FCSTD DOCUMENT  (FreeCAD 0.16R6706 (Git))
Label: Taster_3fach_Unterbau
License: All rights reserved
LicenseURL: http://en.wikipedia.org/wiki/All_rights_reserved
objects: Sketcher::SketchObject×1
note: 1 computed .brp shape members not serialized (recipe doc carries the construction recipe); baked Part::Feature solids carry a one-line shape summary decoded from their .brp

FEATURE [Sketcher::SketchObject] Sketch
  sketch-geometry (51):
    g0: LineSegment StartX=6.07199 StartY=33.4504 StartZ=0 EndX=20.072 EndY=33.4504 EndZ=0
    g1: LineSegment StartX=20.072 StartY=33.4504 StartZ=0 EndX=20.072 EndY=58.5504 EndZ=0
    g2: LineSegment StartX=20.072 StartY=58.5504 StartZ=0 EndX=24.072 EndY=58.5504 EndZ=0
    g3: LineSegment StartX=24.072 StartY=58.5504 StartZ=0 EndX=24.072 EndY=33.4504 EndZ=0
    g4: LineSegment StartX=24.072 StartY=33.4504 StartZ=0 EndX=38.072 EndY=33.4504 EndZ=0
    g5: LineSegment StartX=38.072 StartY=33.4504 StartZ=0 EndX=38.072 EndY=58.5504 EndZ=0
    g6: LineSegment StartX=38.072 StartY=58.5504 StartZ=0 EndX=42.072 EndY=58.5504 EndZ=0
    g7: LineSegment StartX=42.072 StartY=58.5504 StartZ=0 EndX=42.072 EndY=33.4504 EndZ=0
    g8: LineSegment StartX=42.072 StartY=33.4504 StartZ=0 EndX=56.072 EndY=33.4504 EndZ=0
    g9: LineSegment StartX=6.07199 StartY=27.4504 StartZ=0 EndX=20.072 EndY=27.4504 EndZ=0
    g10: LineSegment StartX=20.072 StartY=27.4504 StartZ=0 EndX=20.072 EndY=2.35037 EndZ=0
    g11: LineSegment StartX=20.072 StartY=2.35037 StartZ=0 EndX=24.072 EndY=2.35037 EndZ=0
    g12: LineSegment StartX=24.072 StartY=2.35037 StartZ=0 EndX=24.072 EndY=27.4504 EndZ=0
    g13: LineSegment StartX=24.072 StartY=27.4504 StartZ=0 EndX=38.072 EndY=27.4504 EndZ=0
    g14: LineSegment StartX=38.072 StartY=27.4504 StartZ=0 EndX=38.072 EndY=2.35037 EndZ=0
    g15: LineSegment StartX=38.072 StartY=2.35037 StartZ=0 EndX=42.072 EndY=2.35037 EndZ=0
    g16: LineSegment StartX=42.072 StartY=2.35037 StartZ=0 EndX=42.072 EndY=27.4504 EndZ=0
    g17: LineSegment StartX=42.072 StartY=27.4504 StartZ=0 EndX=56.072 EndY=27.4504 EndZ=0
    g18: LineSegment [constr] StartX=20.072 StartY=33.4504 StartZ=0 EndX=20.072 EndY=27.4504 EndZ=0
    g19: LineSegment StartX=56.072 StartY=33.4504 StartZ=0 EndX=56.072 EndY=45.4504 EndZ=0
    g20: LineSegment StartX=56.072 StartY=27.4504 StartZ=0 EndX=56.072 EndY=15.4504 EndZ=0
    g21: LineSegment StartX=6.07199 StartY=33.4504 StartZ=0 EndX=6.07199 EndY=45.4504 EndZ=0
    g22: LineSegment StartX=6.07199 StartY=27.4504 StartZ=0 EndX=6.07199 EndY=15.4504 EndZ=0
    g23: LineSegment StartX=59.272 StartY=45.4504 StartZ=0 EndX=59.272 EndY=15.4504 EndZ=0
    g24: LineSegment StartX=2.87199 StartY=45.4504 StartZ=0 EndX=2.87199 EndY=15.4504 EndZ=0
    g25: LineSegment [constr] StartX=56.072 StartY=45.4504 StartZ=0 EndX=59.272 EndY=45.4504 EndZ=0
    g26: LineSegment StartX=56.072 StartY=45.4504 StartZ=0 EndX=56.372 EndY=58.5504 EndZ=0
    g27: LineSegment StartX=59.272 StartY=45.4504 StartZ=0 EndX=59.872 EndY=56.9724 EndZ=0
    g28: LineSegment StartX=56.372 StartY=58.5504 StartZ=0 EndX=58.374 EndY=58.5504 EndZ=0
    g29: ArcOfCircle CenterX=58.374 CenterY=57.0504 CenterZ=0 NormalX=0 NormalY=0 NormalZ=1 Radius=1.5 StartAngle=6.23116 EndAngle=7.85398
    g30: LineSegment [constr] StartX=42.072 StartY=58.5504 StartZ=0 EndX=56.372 EndY=58.5504 EndZ=0
    g31: LineSegment StartX=56.072 StartY=15.4504 StartZ=0 EndX=56.372 EndY=2.35037 EndZ=0
    g32: LineSegment StartX=59.272 StartY=15.4504 StartZ=0 EndX=59.872 EndY=3.92838 EndZ=0
    g33: LineSegment StartX=56.372 StartY=2.35037 StartZ=0 EndX=58.374 EndY=2.35037 EndZ=0
    g34: ArcOfCircle CenterX=58.374 CenterY=3.85037 CenterZ=0 NormalX=0 NormalY=0 NormalZ=1 Radius=1.5 StartAngle=4.71239 EndAngle=6.33521
    g35: LineSegment [constr] StartX=42.072 StartY=2.35037 StartZ=0 EndX=56.372 EndY=2.35037 EndZ=0
    g36: LineSegment [constr] StartX=20.072 StartY=2.35037 StartZ=0 EndX=5.77199 EndY=2.35037 EndZ=0
    g37: LineSegment StartX=6.07199 StartY=15.4504 StartZ=0 EndX=5.77199 EndY=2.35037 EndZ=0
    g38: LineSegment StartX=2.87199 StartY=15.4504 StartZ=0 EndX=2.27199 EndY=3.92838 EndZ=0
    g39: LineSegment StartX=6.07199 StartY=45.4504 StartZ=0 EndX=5.77199 EndY=58.5504 EndZ=0
    g40: LineSegment StartX=2.87199 StartY=45.4504 StartZ=0 EndX=2.27199 EndY=56.9724 EndZ=0
    g41: LineSegment StartX=5.77199 StartY=58.5504 StartZ=0 EndX=3.76996 EndY=58.5504 EndZ=0
    g42: LineSegment StartX=5.77199 StartY=2.35037 StartZ=0 EndX=3.76996 EndY=2.35037 EndZ=0
    g43: LineSegment [constr] StartX=20.072 StartY=58.5504 StartZ=0 EndX=5.77199 EndY=58.5504 EndZ=0
    g44: ArcOfCircle CenterX=3.76996 CenterY=3.85037 CenterZ=0 NormalX=0 NormalY=0 NormalZ=1 Radius=1.5 StartAngle=3.08957 EndAngle=4.71239
    g45: ArcOfCircle CenterX=3.76996 CenterY=57.0504 CenterZ=0 NormalX=0 NormalY=0 NormalZ=1 Radius=1.5 StartAngle=1.5708 EndAngle=3.19362
    g46: LineSegment [constr] StartX=2.27199 StartY=56.9724 StartZ=0 EndX=5.80812 EndY=56.9724 EndZ=0
    g47: LineSegment [constr] StartX=59.872 StartY=56.9724 StartZ=0 EndX=56.3358 EndY=56.9724 EndZ=0
    g48: LineSegment [constr] StartX=2.87199 StartY=45.4504 StartZ=0 EndX=6.07199 EndY=45.4504 EndZ=0
    g49: LineSegment [constr] StartX=2.27199 StartY=3.92838 StartZ=0 EndX=5.80812 EndY=3.92838 EndZ=0
    g50: LineSegment [constr] StartX=59.872 StartY=3.92838 StartZ=0 EndX=56.3358 EndY=3.92838 EndZ=0
  constraints (149):
    c: Horizontal(g0)
    c: Coincident(g1,g0)
    c: Vertical(g1)
    c: Coincident(g2,g1)
    c: Coincident(g3,g2)
    c: Vertical(g3)
    c: Coincident(g4,g3)
    c: Coincident(g5,g4)
    c: Vertical(g5)
    c: Coincident(g6,g5)
    c: Coincident(g7,g6)
    c: Vertical(g7)
    c: Coincident(g8,g7)
    c: Horizontal(g6)
    c: Horizontal(g2)
    c: Horizontal(g4)
    c: Horizontal(g8)
    c: Coincident(g10,g9)
    c: Vertical(g10)
    c: Coincident(g11,g10)
    c: Coincident(g12,g11)
    c: Coincident(g13,g12)
    c: Horizontal(g13)
    c: Vertical(g14)
    c: Coincident(g15,g14)
    c: Coincident(g16,g15)
    c: Vertical(g16)
    c: Coincident(g17,g16)
    c: Horizontal(g17)
    c: Horizontal(g15)
    c: Horizontal(g11)
    c: Horizontal(g9)
    c: Equal(g1,g3)
    c: Equal(g3,g5)
    c: Equal(g5,g7)
    c: Equal(g7,g12)
    c: Equal(g12,g10)
    c: Equal(g10,g14)
    c: Equal(g14,g16)
    c: DistanceY(g1,g1) = 25.1
    c: Vertical(g12)
    c: Equal(g2,g6)
    c: Equal(g6,g11)
    c: Equal(g11,g15)
    c: DistanceX(g2,g2) = 4
    c: Equal(g0,g4)
    c: Equal(g4,g8)
    c: Equal(g8,g9)
    c: Equal(g9,g13)
    c: Equal(g13,g17)
    c: DistanceX(g0,g0) = 14
    c: DistanceY(g9,g0) = 6
    c: Coincident(g13,g14)
    c: Coincident(g18,g0)
    c: Coincident(g18,g9)
    c: Vertical(g18)
    c: Coincident(g19,g8)
    c: Vertical(g19)
    c: Coincident(g17,g20)
    c: Vertical(g20)
    c: Coincident(g21,g0)
    c: Vertical(g21)
    c: Coincident(g9,g22)
    c: Vertical(g22)
    c: Equal(g21,g22)
    c: Equal(g22,g19)
    c: Equal(g19,g20)
    c: DistanceY(g21,g21) = 12
    c: Vertical(g23)
    c: Vertical(g24)
    c: Equal(g24,g23)
    c: DistanceY(g24,g24) = 30
    c: Coincident(g25,g19)
    c: Horizontal(g25)
    c: Coincident(g23,g25)
    c: DistanceX(g24,g21) = 3.2
    c: Coincident(g26,g19)
    c: Coincident(g27,g23)
    c: Coincident(g28,g26)
    c: Horizontal(g28)
    c: Coincident(g29,g28)
    c: Coincident(g29,g27)
    c: Radius(g29) = 1.5
    c: Coincident(g30,g6)
    c: Coincident(g30,g26)
    c: Horizontal(g30)
    c: DistanceX(g30,g30) = 14.3
    c: Tangent(g29,g28)
    c: Tangent(g29,g27)
    c: Coincident(g31,g20)
    c: Coincident(g32,g23)
    c: Coincident(g33,g31)
    c: Horizontal(g33)
    c: Coincident(g34,g33)
    c: Coincident(g34,g32)
    c: Coincident(g35,g15)
    c: Coincident(g35,g31)
    c: Horizontal(g35)
    c: Coincident(g36,g10)
    c: Horizontal(g36)
    c: Coincident(g37,g22)
    c: Coincident(g38,g24)
    c: Coincident(g39,g21)
    c: Coincident(g40,g24)
    c: Coincident(g41,g39)
    c: Coincident(g42,g37)
    c: Coincident(g43,g1)
    c: Coincident(g43,g39)
    c: Horizontal(g43)
    c: Horizontal(g42)
    c: Horizontal(g41)
    c: Coincident(g44,g38)
    c: Coincident(g44,g42)
    c: Coincident(g36,g37)
    c: Equal(g36,g43)
    c: Equal(g43,g30)
    c: Equal(g30,g35)
    c: Coincident(g45,g41)
    c: Coincident(g45,g40)
    c: Tangent(g41,g45)
    c: Tangent(g38,g44)
    c: Tangent(g42,g44)
    c: Tangent(g40,g45)
    c: Tangent(g34,g32)
    c: Equal(g33,g34)
    c: Tangent(g34,g33)
    c: Equal(g29,g34)
    c: Equal(g34,g44)
    c: Equal(g44,g45)
    c: DistanceX(g40,g27) = 57.6
    c: PointOnObject(g46,g39)
    c: Horizontal(g46)
    c: Coincident(g40,g46)
    c: Coincident(g47,g27)
    c: PointOnObject(g47,g26)
    c: Horizontal(g47)
    c: Equal(g47,g46)
    c: Coincident(g48,g24)
    c: Coincident(g48,g21)
    c: Horizontal(g48)
    c: DistanceX(g38,g32) = 57.6
    c: PointOnObject(g49,g37)
    c: Horizontal(g49)
    c: Coincident(g50,g32)
    c: PointOnObject(g50,g31)
    c: Horizontal(g50)
    c: Equal(g50,g49)
    c: Coincident(g38,g49)
    c: Equal(g25,g48)
